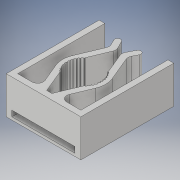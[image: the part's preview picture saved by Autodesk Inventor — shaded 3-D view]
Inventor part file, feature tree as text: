
AUTODESK INVENTOR PART (.ipt)
format: ipt  version: 2019.3 (Build 233278000, 278)  size: 1,121,792 bytes
history: native  units: mm
features: extrude x4, sketch x3, mirror x1, projected_geometry x1
ambient origin geometry x8: Origin, YZ Plane, XZ Plane, XY Plane, X Axis, Y Axis, Z Axis, Center Point
bodies: Body1 (feature_tree)
feature tree (9):
  extrude  "Extrusion2"  Depth=0.5mm
  extrude  "Extrusion4"  Depth=0.5mm
  mirror  "Mirror1"
  extrude  "Extrusion5"  Depth=1.0mm
  extrude  "Extrusion6"  TaperAngle=30.0deg  [1 undecoded]
  sketch  "Sketch2"  dims[d3=5.047545mm d4=0.5mm]
  projected_geometry  "Projected Loop1"
  sketch  "Sketch3"  dims[d5=0.5mm d6=0.5mm]
  sketch  "Sketch4"  dims[d7=60.0deg d8=0.5mm d9=30.0deg d10=400.0mm d12=360.0deg d14=10.0mm d15=0.0mm d16=0.15mm d17=15.0mm d20=22.68928mm d21=2.0mm d22=2.0mm d23=10.0mm d24=10.0mm d25=2.0mm d26=4.0mm d27=2.0mm d28=1.0mm d29=2.0mm d30=2.0mm d31=3.0mm d32=11.0mm d34=10.0mm d35=0.0mm d36=2.0mm d37=0.0mm d38=1.0mm d39=0.0mm]
note: 1 required parameter value undecoded (feature->parameter linkage not recoverable at this tier; creation-order binding heuristic only, values carry confidence <= 0.55)
